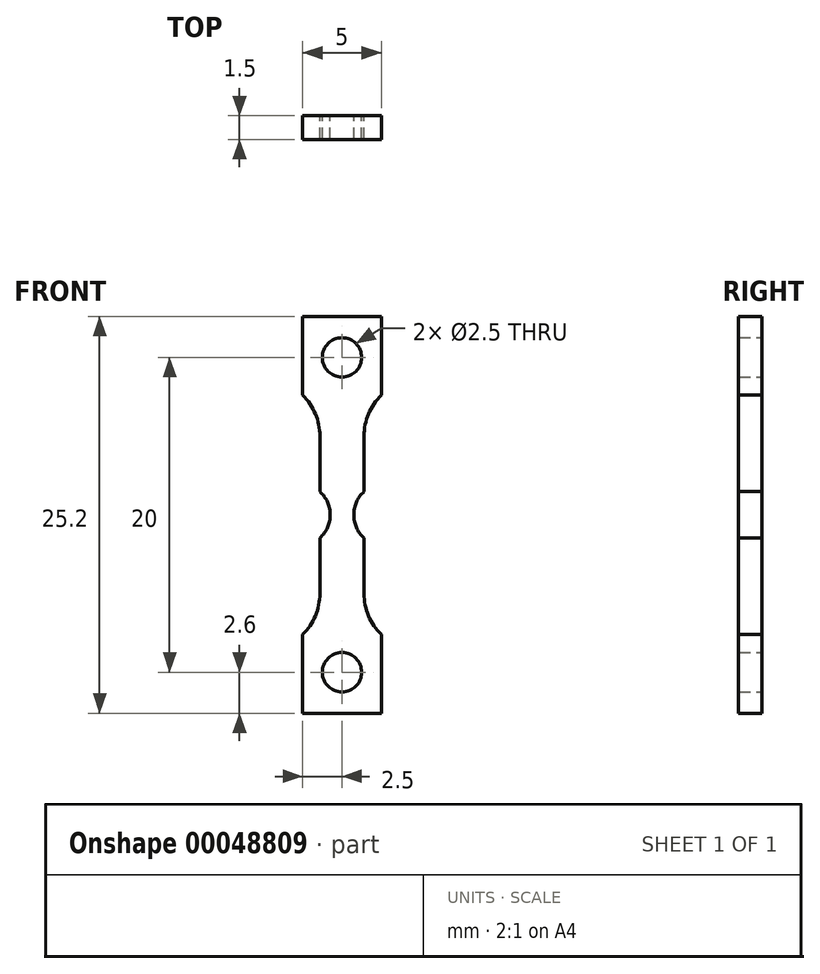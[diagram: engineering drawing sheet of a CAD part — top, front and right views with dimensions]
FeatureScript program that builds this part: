
annotation { "Feature Type Name" : "Feature", "Feature Type Description" : "" }
export const myFeature = defineFeature(function(context is Context, id is Id, definition is map)
    precondition{}
    {
        {
            assignVariable(context, id + "F0", {"variableType" : VariableType.LENGTH, "name" : "thickness", "lengthValue" : 1.5 * mm});
        }
        {
            var Q0;
            Q0=qCreatedBy(makeId("Front.planeOp"),FACE);
            var sketch = newSketch(context, id + "F1", { "sketchPlane" : qUnion([Q0])});
            skPoint(sketch, "E0.middle", {"position": v(0, 0) * mm});
            skLineSegment(sketch, "E1", {"start": v(1.4, 0) * mm, "end": v(1.4, 5) * mm});
            skLineSegment(sketch, "E2", {"start": v(2.5, 12.6) * mm, "end": v(2.5, 7.6) * mm});
            skArc(sketch, "E3", {"start": v(1.4, 5) * mm, "mid": v(1.69, 6.41) * mm, "end": v(2.5, 7.6) * mm});
            skLineSegment(sketch, "E4", {"start": v(2.5, 12.6) * mm, "end": v(0, 12.6) * mm});
            skLineSegment(sketch, "E5.MirrorCS", {"start": v(-2.5, 12.6) * mm, "end": v(0, 12.6) * mm});
            skLineSegment(sketch, "E6.MirrorCS", {"start": v(-2.5, 12.6) * mm, "end": v(-2.5, 7.6) * mm});
            skArc(sketch, "E7.MirrorCS", {"start": v(-1.4, 5) * mm, "mid": v(-1.69, 6.41) * mm, "end": v(-2.5, 7.6) * mm});
            skLineSegment(sketch, "E8.MirrorCS", {"start": v(-1.4, 0) * mm, "end": v(-1.4, 5) * mm});
            skLineSegment(sketch, "E9.MirrorCS", {"start": v(1.4, 0) * mm, "end": v(1.4, -5) * mm});
            skArc(sketch, "E10.MirrorCS", {"start": v(1.4, -5) * mm, "mid": v(1.69, -6.41) * mm, "end": v(2.5, -7.6) * mm});
            skLineSegment(sketch, "E11.MirrorCS", {"start": v(2.5, -12.6) * mm, "end": v(2.5, -7.6) * mm});
            skLineSegment(sketch, "E12.MirrorCS", {"start": v(2.5, -12.6) * mm, "end": v(0, -12.6) * mm});
            skLineSegment(sketch, "E13.MirrorCS", {"start": v(-2.5, -12.6) * mm, "end": v(0, -12.6) * mm});
            skLineSegment(sketch, "E14.MirrorCS", {"start": v(-2.5, -12.6) * mm, "end": v(-2.5, -7.6) * mm});
            skArc(sketch, "E15.MirrorCS", {"start": v(-1.4, -5) * mm, "mid": v(-1.69, -6.41) * mm, "end": v(-2.5, -7.6) * mm});
            skLineSegment(sketch, "E16.MirrorCS", {"start": v(-1.4, 0) * mm, "end": v(-1.4, -5) * mm});
            skPoint(sketch, "E17", {"position": v(0, 10) * mm});
            skCircle(sketch, "E18", {"center": v(0, 10) * mm, "radius": 1.25 * mm});
            skCircle(sketch, "E19.MirrorC", {"center": v(0, -10) * mm, "radius": 1.25 * mm});
            skLineSegment(sketch, "E20", {"start": v(1.4, 0) * mm, "end": v(-1.4, 0) * mm, "construction": true});
            skPoint(sketch, "E21", {"position": v(-0.75, 0) * mm});
            skPoint(sketch, "E22", {"position": v(-2.75, 0) * mm});
            skArc(sketch, "E23", {"start": v(-0.75, 0) * mm, "mid": v(-0.92, 0.8) * mm, "end": v(-1.4, 1.48) * mm});
            skArc(sketch, "E24.MirrorCS", {"start": v(-0.75, 0) * mm, "mid": v(-0.92, -0.8) * mm, "end": v(-1.4, -1.48) * mm});
            skArc(sketch, "E25.MirrorCS", {"start": v(0.75, 0) * mm, "mid": v(0.92, 0.8) * mm, "end": v(1.4, 1.48) * mm});
            skArc(sketch, "E26.MirrorCS", {"start": v(0.75, 0) * mm, "mid": v(0.92, -0.8) * mm, "end": v(1.4, -1.48) * mm});
            skSolve(sketch);
        }
        {
            var Q0;
            Q0=makeQuery(id+"F1.imprint","IMPRINT",FACE,{"disambiguationData":[TD([[makeQuery(id+"F1.imprint","IMPRINT",EDGE,{"derivedFrom":sQuery(id+"F1.wireOp",EDGE,"E2")}),-1.0]])]});
            extrude(context, id + "F2", {"entities" : qUnion([Q0]), "offsetDistance" : 25 * mm, "depth" : getVariable(context, 'thickness'), "symmetric" : true});
        }
    });
